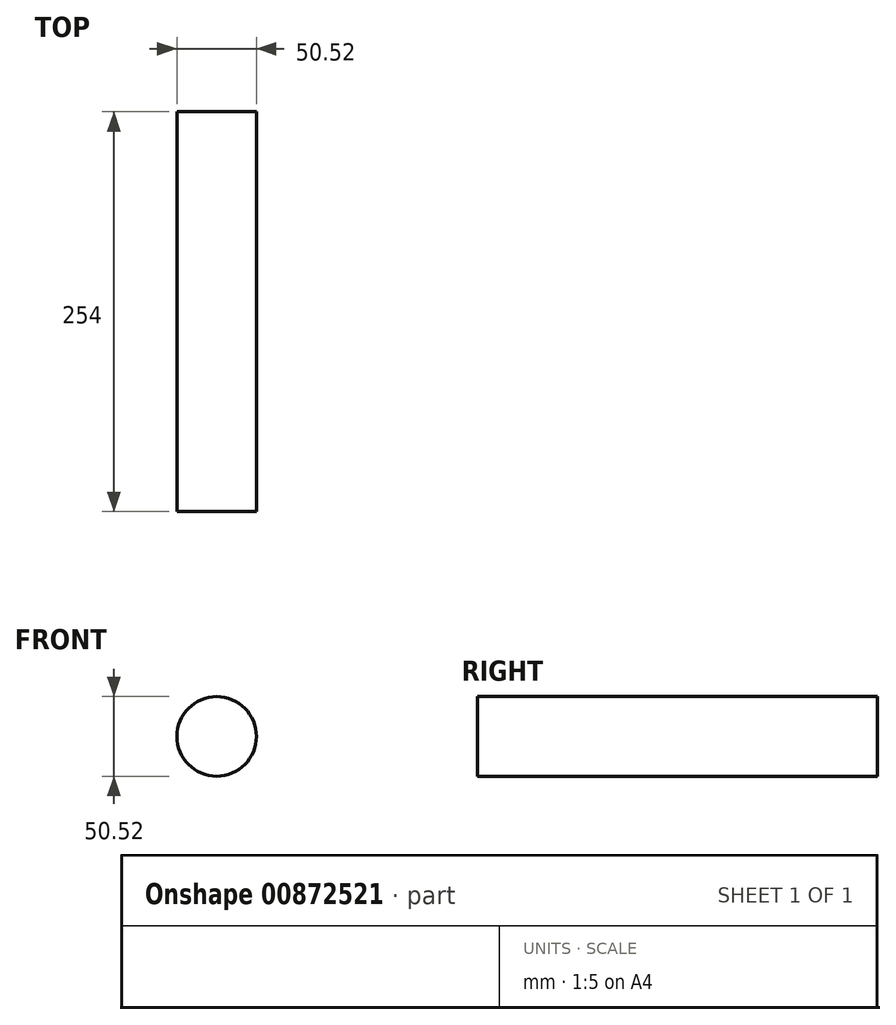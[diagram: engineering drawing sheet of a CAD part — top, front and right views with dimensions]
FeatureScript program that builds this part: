
annotation { "Feature Type Name" : "Feature", "Feature Type Description" : "" }
export const myFeature = defineFeature(function(context is Context, id is Id, definition is map)
    precondition{}
    {
        {
            var Q0;
            Q0=qCreatedBy(makeId("Front.planeOp"),FACE);
            var sketch = newSketch(context, id + "F0", { "sketchPlane" : qUnion([Q0])});
            skCircle(sketch, "E0", {"center": v(0, 0) * mm, "radius": 25.26 * mm});
            skSolve(sketch);
        }
        {
            var Q0;
            Q0 = qSketchRegion(id + "F0", true);
            extrude(context, id + "F1", {"entities" : qUnion([Q0]), "depth" : 254 * mm, "offsetDistance" : 25.4 * mm});
        }
    });
